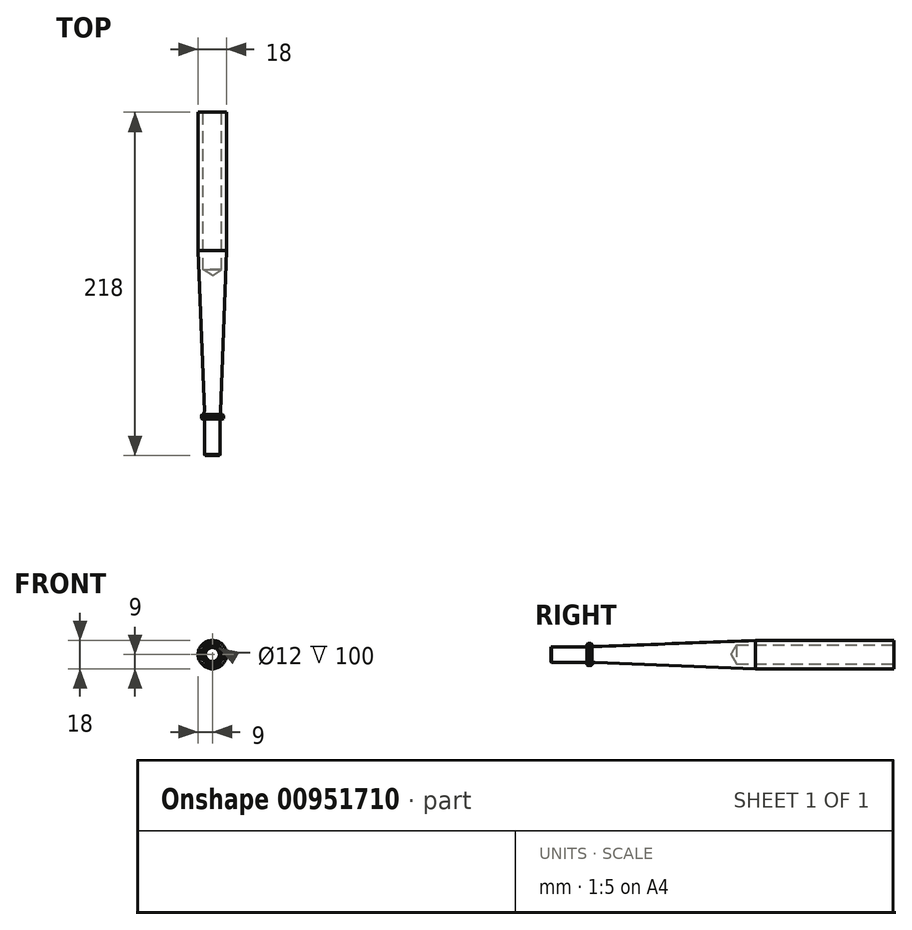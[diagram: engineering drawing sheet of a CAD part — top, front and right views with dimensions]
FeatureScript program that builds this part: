
annotation { "Feature Type Name" : "Feature", "Feature Type Description" : "" }
export const myFeature = defineFeature(function(context is Context, id is Id, definition is map)
    precondition{}
    {
        {
            var Q0;
            Q0=qCreatedBy(makeId("Right.planeOp"),FACE);
            var sketch = newSketch(context, id + "F0", { "sketchPlane" : qUnion([Q0])});
            skLineSegment(sketch, "E0.top", {"start": v(103.6, 9) * mm, "end": v(15.6, 9) * mm});
            skLineSegment(sketch, "E1", {"start": v(-114.4, 0) * mm, "end": v(-114.4, 5) * mm});
            skLineSegment(sketch, "E2", {"start": v(-114.4, 5) * mm, "end": v(-91.4, 5) * mm});
            skLineSegment(sketch, "E3", {"start": v(-91.4, 5) * mm, "end": v(-91.4, 7) * mm});
            skLineSegment(sketch, "E4", {"start": v(-91.4, 7) * mm, "end": v(-88.4, 7) * mm});
            skLineSegment(sketch, "E5", {"start": v(-88.4, 7) * mm, "end": v(-88.4, 5) * mm});
            skLineSegment(sketch, "E6.top", {"start": v(103.6, 6) * mm, "end": v(3.6, 6) * mm});
            skLineSegment(sketch, "E7", {"start": v(3.6, 6) * mm, "end": v(0, 0) * mm});
            skLineSegment(sketch, "E8.trimOffspring", {"start": v(0, 0) * mm, "end": v(-114.4, 0) * mm});
            skLineSegment(sketch, "E9", {"start": v(-88.4, 5) * mm, "end": v(15.6, 9) * mm});
            skLineSegment(sketch, "E10", {"start": v(103.6, 9) * mm, "end": v(103.6, 6) * mm});
            skSolve(sketch);
        }
        {
            var Q0;
            Q0=makeQuery(id+"F0.imprint","IMPRINT",FACE,{"disambiguationData":[TD([[makeQuery(id+"F0.imprint","IMPRINT",EDGE,{"derivedFrom":sQuery(id+"F0.wireOp",EDGE,"E0.top")}),1.0]])]});
            var Q1;
            Q1=sQuery(id+"F0.wireOp",EDGE,"E8.trimOffspring");
            revolve(context, id + "F1", {"surfaceOperationType" : NewSurfaceOperationType.NEW, "entities" : qUnion([Q0]), "axis" : qUnion([Q1]), "revolveType" : RevolveType.FULL});
        }
        {
            var Q0;
            Q0=makeQuery(id+"F1.opRevolve","SWEPT_EDGE",EDGE,{"disambiguationData":[OSD([sQuery(id+"F0.wireOp",EDGE,"E3"),sQuery(id+"F0.wireOp",EDGE,"E4")])]});
            var Q1;
            Q1=makeQuery(id+"F1.opRevolve","SWEPT_EDGE",EDGE,{"disambiguationData":[OSD([sQuery(id+"F0.wireOp",EDGE,"E4"),sQuery(id+"F0.wireOp",EDGE,"E5")])]});
            var Q2;
            Q2=makeQuery(id+"F1.opRevolve","SWEPT_EDGE",EDGE,{"disambiguationData":[OSD([sQuery(id+"F0.wireOp",EDGE,"E1"),sQuery(id+"F0.wireOp",EDGE,"E2")])]});
            chamfer(context, id + "F2", {"entities" : qUnion([Q0, Q1, Q2]), "width" : 0.5 * mm, "tangentPropagation" : true});
        }
        {
            var Q0;
            Q0=makeQuery(id+"F1.opRevolve","SWEPT_EDGE",EDGE,{"disambiguationData":[OSD([sQuery(id+"F0.wireOp",EDGE,"E5"),sQuery(id+"F0.wireOp",EDGE,"E9")])]});
            fillet(context, id + "F3", {"entities" : qUnion([Q0]), "radius" : 2 * mm, "tangentPropagation" : true, "allowEdgeOverflow" : false});
        }
    });
